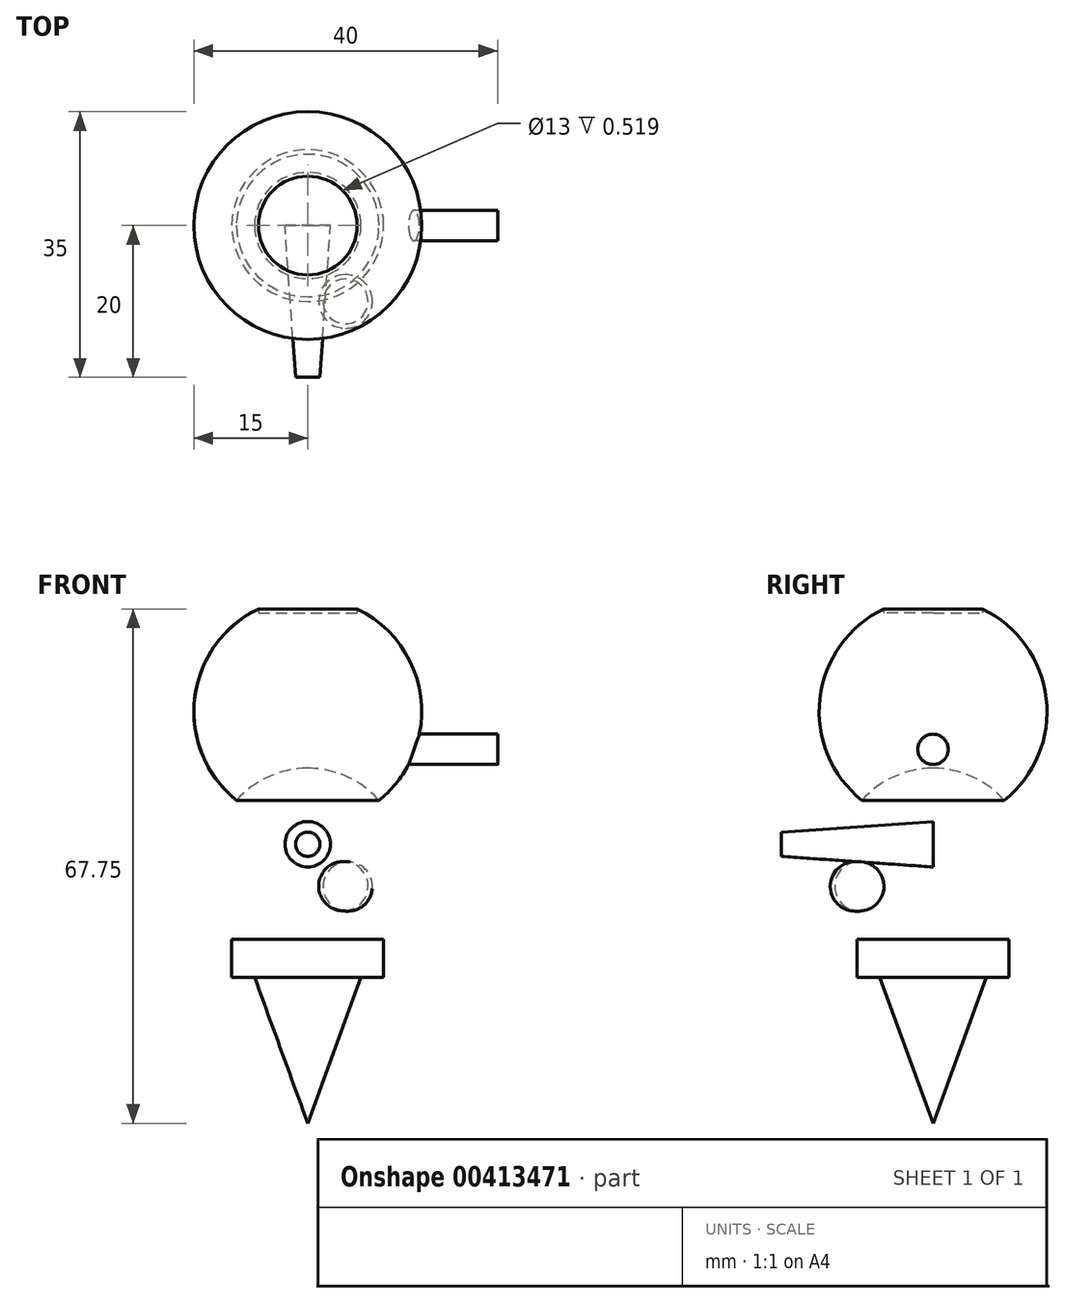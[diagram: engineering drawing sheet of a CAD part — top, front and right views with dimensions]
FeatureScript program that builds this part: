
annotation { "Feature Type Name" : "Feature", "Feature Type Description" : "" }
export const myFeature = defineFeature(function(context is Context, id is Id, definition is map)
    precondition{}
    {
        {
            var Q0;
            Q0=qCreatedBy(makeId("Front.planeOp"),FACE);
            var sketch = newSketch(context, id + "F0", { "sketchPlane" : qUnion([Q0])});
            skCircle(sketch, "E0", {"center": v(0, 0) * mm, "radius": 15 * mm});
            skCircle(sketch, "E1", {"center": v(0, -19.96) * mm, "radius": 12.5 * mm});
            skLineSegment(sketch, "E2", {"start": v(0, 15) * mm, "end": v(0, -32.46) * mm});
            skSolve(sketch);
        }
        {
            var Q0;
            {var subQ0=sQuery(id+"F0.wireOp",EDGE,"E2");var subQ1=sQuery(id+"F0.wireOp",EDGE,"E0");var subQ2=makeQuery(id+"F0.imprint","INTERSECT",VERTEX,{"disambiguationData":[OD(0.0)],"derivedFrom":[subQ1,subQ0]});Q0=makeQuery(id+"F0.imprint","IMPRINT",FACE,{"disambiguationData":[TD([[makeQuery(id+"F0.imprint","IMPRINT",EDGE,{"disambiguationData":[TD([[subQ2,-1.0]])],"derivedFrom":subQ1}),1.0]])]});}
            var Q1;
            {var subQ0=sQuery(id+"F0.wireOp",EDGE,"E1");var subQ1=sQuery(id+"F0.wireOp",EDGE,"E0");var subQ2=makeQuery(id+"F0.imprint","INTERSECT",VERTEX,{"disambiguationData":[OD(0.0)],"derivedFrom":[subQ1,subQ0]});Q1=makeQuery(id+"F0.imprint","IMPRINT",FACE,{"disambiguationData":[TD([[makeQuery(id+"F0.imprint","IMPRINT",EDGE,{"disambiguationData":[TD([[subQ2,-1.0]])],"derivedFrom":subQ1}),-1.0]])]});}
            var Q2;
            Q2=sQuery(id+"F0.wireOp",EDGE,"E2");
            revolve(context, id + "F1", {"entities" : qUnion([Q0, Q1]), "axis" : qUnion([Q2]), "revolveType" : RevolveType.FULL});
        }
        {
            var Q0;
            Q0=qCreatedBy(makeId("Top.planeOp"),FACE);
            cPlane(context, id + "F2", {"entities" : qUnion([Q0]), "cplaneType" : CPlaneType.OFFSET, "offset" : 13 * mm, "width" : 150 * mm, "height" : 150 * mm});
        }
        {
            var Q0;
            Q0=qCreatedBy(id+"F2.planeOp",FACE);
            var sketch = newSketch(context, id + "F3", { "sketchPlane" : qUnion([Q0])});
            skCircle(sketch, "E3", {"center": v(0, 0) * mm, "radius": 6.5 * mm});
            skSolve(sketch);
        }
        {
            var Q0;
            Q0 = qSketchRegion(id + "F3", true);
            extrude(context, id + "F4", {"entities" : qUnion([Q0]), "operationType" : NewBodyOperationType.REMOVE, "depth" : 25 * mm});
        }
        {
            var Q0;
            Q0=qCreatedBy(makeId("Front.planeOp"),FACE);
            var sketch = newSketch(context, id + "F5", { "sketchPlane" : qUnion([Q0])});
            skCircle(sketch, "E4", {"center": v(0, -17.47) * mm, "radius": 3 * mm});
            skSolve(sketch);
        }
        {
            var Q0;
            Q0 = qSketchRegion(id + "F5", true);
            extrude(context, id + "F6", {"entities" : qUnion([Q0]), "operationType" : NewBodyOperationType.ADD, "depth" : 20 * mm, "hasDraft" : true, "draftAngle" : 4 * degree, "draftPullDirection" : true});
        }
        {
            var Q0;
            Q0=qCreatedBy(makeId("Front.planeOp"),FACE);
            cPlane(context, id + "F7", {"entities" : qUnion([Q0]), "cplaneType" : CPlaneType.OFFSET, "offset" : 10 * mm, "width" : 150 * mm, "height" : 150 * mm});
        }
        {
            var Q0;
            Q0=qCreatedBy(id+"F7.planeOp",FACE);
            var sketch = newSketch(context, id + "F8", { "sketchPlane" : qUnion([Q0])});
            skCircle(sketch, "E5", {"center": v(5.26, -23.04) * mm, "radius": 3.25 * mm});
            skLineSegment(sketch, "E6", {"start": v(4.7, -26.24) * mm, "end": v(5.26, -19.8) * mm});
            skPoint(sketch, "E7", {"position": v(0, -23.04) * mm});
            skLineSegment(sketch, "E8", {"start": v(5.26, -23.04) * mm, "end": v(4.97, -23.04) * mm});
            skPoint(sketch, "E9", {"position": v(-5.26, -23.04) * mm});
            skSolve(sketch);
        }
        {
            var Q0;
            {var subQ0=sQuery(id+"F8.wireOp",EDGE,"E6");var subQ4=makeQuery(id+"F8.imprint","IMPRINT",VERTEX,{"derivedFrom":subQ0});Q0=makeQuery(id+"F8.imprint","IMPRINT",FACE,{"disambiguationData":[TD([[makeQuery(id+"F8.imprint","IMPRINT",EDGE,{"disambiguationData":[TD([[subQ4,1.0]])],"derivedFrom":subQ0}),-1.0]])]});}
            var Q1;
            Q1=sQuery(id+"F8.wireOp",EDGE,"E6");
            revolve(context, id + "F9", {"operationType" : NewBodyOperationType.ADD, "entities" : qUnion([Q0]), "axis" : qUnion([Q1]), "revolveType" : RevolveType.FULL, "oppositeDirection" : true});
        }
        {
            var Q0;
            Q0=qCreatedBy(makeId("Top.planeOp"),FACE);
            cPlane(context, id + "F10", {"entities" : qUnion([Q0]), "cplaneType" : CPlaneType.OFFSET, "offset" : 30 * mm, "oppositeDirection" : true, "width" : 150 * mm, "height" : 150 * mm});
        }
        {
            var Q0;
            Q0=qCreatedBy(id+"F10.planeOp",FACE);
            var sketch = newSketch(context, id + "F11", { "sketchPlane" : qUnion([Q0])});
            skCircle(sketch, "E10", {"center": v(0, 0) * mm, "radius": 10 * mm});
            skSolve(sketch);
        }
        {
            var Q0;
            Q0 = qSketchRegion(id + "F11", true);
            extrude(context, id + "F12", {"entities" : qUnion([Q0]), "oppositeDirection" : true, "depth" : 5 * mm});
        }
        {
            var Q0;
            Q0=qCreatedBy(makeId("Top.planeOp"),FACE);
            cPlane(context, id + "F13", {"entities" : qUnion([Q0]), "cplaneType" : CPlaneType.OFFSET, "offset" : 35 * mm, "oppositeDirection" : true, "width" : 150 * mm, "height" : 150 * mm});
        }
        {
            var Q0;
            Q0=qCreatedBy(id+"F13.planeOp",FACE);
            var sketch = newSketch(context, id + "F14", { "sketchPlane" : qUnion([Q0])});
            skCircle(sketch, "E11", {"center": v(0, 0) * mm, "radius": 7 * mm});
            skSolve(sketch);
        }
        {
            var Q0;
            Q0 = qSketchRegion(id + "F14", true);
            extrude(context, id + "F15", {"entities" : qUnion([Q0]), "operationType" : NewBodyOperationType.ADD, "oppositeDirection" : true, "depth" : 25 * mm, "hasDraft" : true, "draftAngle" : 20 * degree, "draftPullDirection" : true});
        }
        {
            var Q0;
            Q0=qCreatedBy(makeId("Right.planeOp"),FACE);
            var sketch = newSketch(context, id + "F16", { "sketchPlane" : qUnion([Q0])});
            skCircle(sketch, "E12", {"center": v(0, -4.98) * mm, "radius": 2 * mm});
            skSolve(sketch);
        }
        {
            var Q0;
            Q0 = qSketchRegion(id + "F16", true);
            extrude(context, id + "F17", {"entities" : qUnion([Q0]), "operationType" : NewBodyOperationType.ADD, "depth" : 25 * mm});
        }
    });
